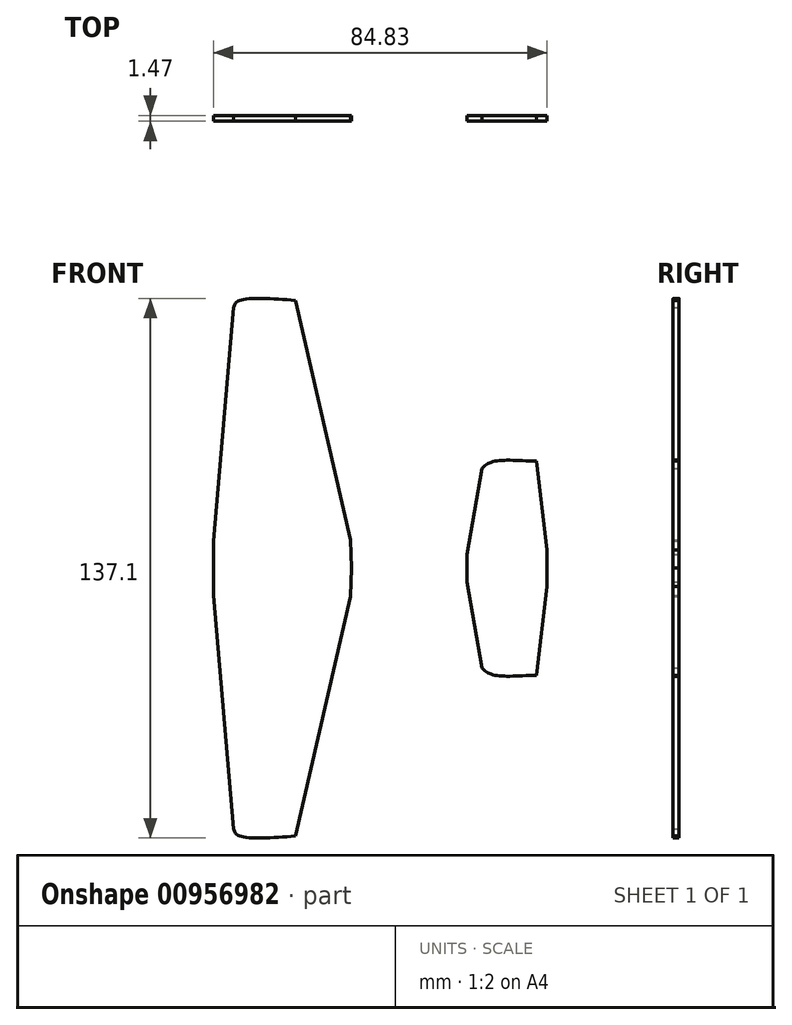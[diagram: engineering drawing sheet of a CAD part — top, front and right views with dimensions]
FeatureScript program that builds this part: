
annotation { "Feature Type Name" : "Feature", "Feature Type Description" : "" }
export const myFeature = defineFeature(function(context is Context, id is Id, definition is map)
    precondition{}
    {
        {
            var Q0;
            Q0=qCreatedBy(makeId("Front.planeOp"),FACE);
            var sketch = newSketch(context, id + "F0", { "sketchPlane" : qUnion([Q0])});
            skLineSegment(sketch, "E0.bottom", {"start": v(50.8, 114.3) * mm, "end": v(-50.8, 114.3) * mm, "construction": true});
            skLineSegment(sketch, "E0.top", {"start": v(50.8, -114.3) * mm, "end": v(-50.8, -114.3) * mm, "construction": true});
            skLineSegment(sketch, "E0.left", {"start": v(50.8, 114.3) * mm, "end": v(50.8, -114.3) * mm, "construction": true});
            skLineSegment(sketch, "E0.right", {"start": v(-50.8, 114.3) * mm, "end": v(-50.8, -114.3) * mm, "construction": true});
            skPoint(sketch, "E0.middle", {"position": v(0, 0) * mm});
            skLineSegment(sketch, "E1", {"start": v(-46.03, 0) * mm, "end": v(-10.87, 0) * mm, "construction": true});
            skLineSegment(sketch, "E2", {"start": v(18.4, 0) * mm, "end": v(38.8, 0) * mm, "construction": true});
            skLineSegment(sketch, "E3", {"start": v(-46.03, 0) * mm, "end": v(-46.03, 6.98) * mm});
            skLineSegment(sketch, "E4", {"start": v(-46.03, 6.98) * mm, "end": v(-40.95, 66.25) * mm});
            skFitSpline(sketch, "E5", {"points": [v(-40.95, 66.25) * mm, v(-39.58, 67.92) * mm, v(-25.15, 68.04) * mm], "startDerivative": vector(2.78, 6.8) * mm, "endDerivative": vector(25.47, -1.92) * mm});
            skLineSegment(sketch, "E6", {"start": v(-25.15, 68.04) * mm, "end": v(-11.12, 7.21) * mm});
            skLineSegment(sketch, "E7", {"start": v(-11.12, 7.21) * mm, "end": v(-10.87, 0) * mm});
            skLineSegment(sketch, "E8.MirrorCS", {"start": v(-11.12, -7.21) * mm, "end": v(-10.87, 0) * mm});
            skLineSegment(sketch, "E9.MirrorCS", {"start": v(-25.15, -68.04) * mm, "end": v(-11.12, -7.21) * mm});
            skFitSpline(sketch, "E10.MirrorCS", {"points": [v(-40.95, -66.25) * mm, v(-39.58, -67.92) * mm, v(-25.15, -68.04) * mm], "startDerivative": vector(2.78, -6.8) * mm, "endDerivative": vector(25.47, 1.92) * mm});
            skLineSegment(sketch, "E11.MirrorCS", {"start": v(-46.03, 0) * mm, "end": v(-46.03, -6.98) * mm});
            skLineSegment(sketch, "E12.MirrorCS", {"start": v(-46.03, -6.98) * mm, "end": v(-40.95, -66.25) * mm});
            skLineSegment(sketch, "E13", {"start": v(18.4, 0) * mm, "end": v(18.4, 3.45) * mm});
            skPoint(sketch, "E13.endSnap0", {"position": v(47.13, 3.45) * mm});
            skLineSegment(sketch, "E14", {"start": v(18.4, 3.45) * mm, "end": v(22.2, 25.34) * mm});
            skFitSpline(sketch, "E15", {"points": [v(22.2, 25.34) * mm, v(25.12, 27.09) * mm, v(36.08, 27.2) * mm], "startDerivative": vector(5.7, 6.09) * mm, "endDerivative": vector(21.2, -0.67) * mm});
            skLineSegment(sketch, "E16", {"start": v(36.08, 27.2) * mm, "end": v(38.77, 4.63) * mm});
            skLineSegment(sketch, "E17", {"start": v(38.77, 4.63) * mm, "end": v(38.8, 0) * mm});
            skLineSegment(sketch, "E18.MirrorCS", {"start": v(18.4, 0) * mm, "end": v(18.4, -3.45) * mm});
            skLineSegment(sketch, "E19.MirrorCS", {"start": v(18.4, -3.45) * mm, "end": v(22.2, -25.34) * mm});
            skFitSpline(sketch, "E20.MirrorCS", {"points": [v(22.2, -25.34) * mm, v(25.12, -27.09) * mm, v(36.08, -27.2) * mm], "startDerivative": vector(5.7, -6.09) * mm, "endDerivative": vector(21.2, 0.67) * mm});
            skLineSegment(sketch, "E21.MirrorCS", {"start": v(38.77, -4.63) * mm, "end": v(38.8, 0) * mm});
            skLineSegment(sketch, "E22.MirrorCS", {"start": v(36.08, -27.2) * mm, "end": v(38.77, -4.63) * mm});
            skSolve(sketch);
        }
        {
            var Q0;
            Q0=makeQuery(id+"F0.imprint","IMPRINT",FACE,{"disambiguationData":[TD([[makeQuery(id+"F0.imprint","IMPRINT",EDGE,{"derivedFrom":sQuery(id+"F0.wireOp",EDGE,"E3")}),-1.0]])]});
            var Q1;
            Q1=makeQuery(id+"F0.imprint","IMPRINT",FACE,{"disambiguationData":[TD([[makeQuery(id+"F0.imprint","IMPRINT",EDGE,{"derivedFrom":sQuery(id+"F0.wireOp",EDGE,"E13")}),-1.0]])]});
            extrude(context, id + "F1", {"entities" : qUnion([Q0, Q1]), "depth" : 1.47 * mm, "offsetDistance" : 25.4 * mm});
        }
        {
            var Q0;
            Q0 = qSketchRegion(id + "F0", true);
            extrude(context, id + "F2", {"entities" : qUnion([Q0]), "depth" : 1.47 * mm, "offsetDistance" : 25.4 * mm});
        }
    });
